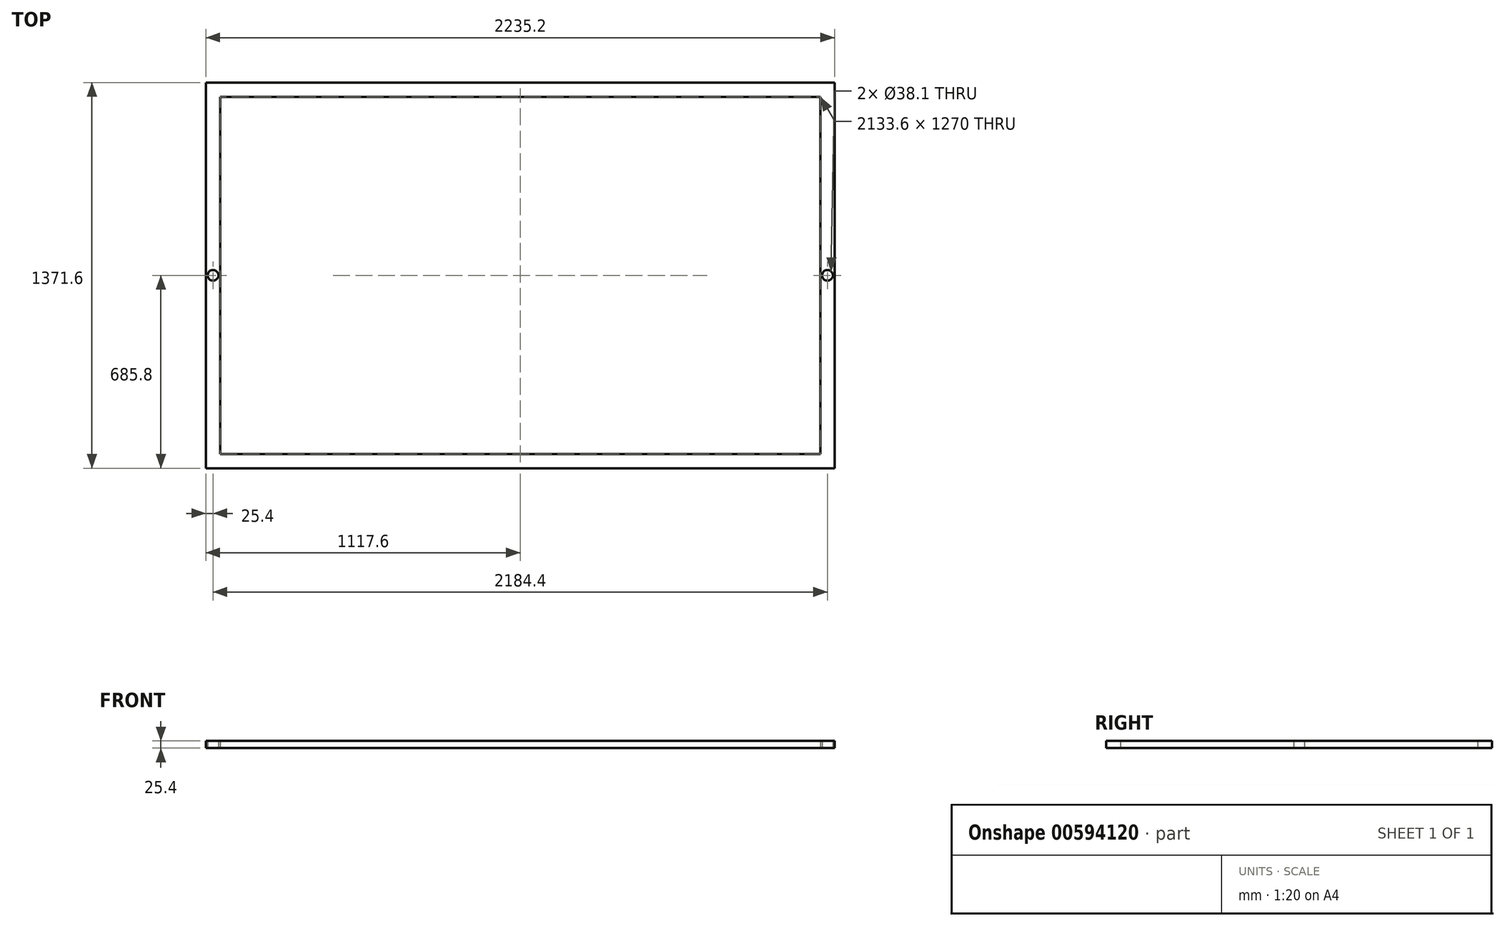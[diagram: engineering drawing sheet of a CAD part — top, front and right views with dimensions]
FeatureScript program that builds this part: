
annotation { "Feature Type Name" : "Feature", "Feature Type Description" : "" }
export const myFeature = defineFeature(function(context is Context, id is Id, definition is map)
    precondition{}
    {
        {
            var Q0;
            Q0=qCreatedBy(makeId("Top.planeOp"),FACE);
            var sketch = newSketch(context, id + "F0", { "sketchPlane" : qUnion([Q0])});
            skLineSegment(sketch, "E0.bottom", {"start": v(-1066.8, -635) * mm, "end": v(1066.8, -635) * mm});
            skLineSegment(sketch, "E0.top", {"start": v(-1066.8, 635) * mm, "end": v(1066.8, 635) * mm});
            skLineSegment(sketch, "E0.left", {"start": v(-1066.8, -635) * mm, "end": v(-1066.8, 635) * mm});
            skLineSegment(sketch, "E0.right", {"start": v(1066.8, -635) * mm, "end": v(1066.8, 635) * mm});
            skPoint(sketch, "E0.middle", {"position": v(0, 0) * mm});
            skLineSegment(sketch, "E1.bottom", {"start": v(-1117.6, -685.8) * mm, "end": v(1117.6, -685.8) * mm});
            skLineSegment(sketch, "E1.top", {"start": v(-1117.6, 685.8) * mm, "end": v(1117.6, 685.8) * mm});
            skLineSegment(sketch, "E1.left", {"start": v(-1117.6, -685.8) * mm, "end": v(-1117.6, 685.8) * mm});
            skLineSegment(sketch, "E1.right", {"start": v(1117.6, -685.8) * mm, "end": v(1117.6, 685.8) * mm});
            skCircle(sketch, "E2", {"center": v(-1092.2, 0) * mm, "radius": 19.05 * mm});
            skCircle(sketch, "E3", {"center": v(1092.2, 0) * mm, "radius": 19.05 * mm});
            skPoint(sketch, "E4.start.orphan", {"position": v(-1117.6, 0) * mm});
            skPoint(sketch, "E5.trimOffspring.end.orphan", {"position": v(-1066.8, 0) * mm});
            skPoint(sketch, "E6.start.orphan", {"position": v(1066.8, 0) * mm});
            skPoint(sketch, "E7.trimOffspring.end.orphan", {"position": v(1117.6, 0) * mm});
            skSolve(sketch);
        }
        {
            var Q0;
            Q0=makeQuery(id+"F0.imprint","IMPRINT",FACE,{"disambiguationData":[TD([[makeQuery(id+"F0.imprint","IMPRINT",EDGE,{"derivedFrom":sQuery(id+"F0.wireOp",EDGE,"E0.bottom")}),1.0]])]});
            extrude(context, id + "F1", {"entities" : qUnion([Q0]), "depth" : 25.4 * mm, "offsetDistance" : 25.4 * mm});
        }
        {
            var Q0;
            Q0=makeQuery(id+"F0.imprint","IMPRINT",FACE,{"disambiguationData":[TD([[makeQuery(id+"F0.imprint","IMPRINT",EDGE,{"derivedFrom":sQuery(id+"F0.wireOp",EDGE,"E0.bottom")}),-1.0]])]});
            extrude(context, id + "F2", {"entities" : qUnion([Q0]), "depth" : 25.4 * mm, "offsetDistance" : 25.4 * mm});
        }
    });
